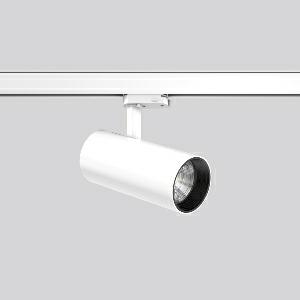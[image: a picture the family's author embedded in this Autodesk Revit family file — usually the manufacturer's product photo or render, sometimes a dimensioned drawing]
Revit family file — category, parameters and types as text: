
# Revit family: deecos_s_mini_742208_002_b176
name_source: partatom
category: Lighting Fixtures
units: mm (PartAtom-declared; Revit-internal decimal feet)

## family parameters
Cut with Voids When Loaded = No
Host = Face
Light Source = No
Part Type = Normal
Room Calculation Point = No
Round Connector Dimension = Use Diameter
Shared = No

## types (1)
- DEECOS S mini (1 x LED Modul 930, 2850 lm, 3000)
    Apparent Load = 29 VA
    Approval mark = CE
    CIE Flux Codes = 98 100 100 100 100
    Color Rendering = 90
    Color Temperature = 3000
    Default Elevation = 1800 mm
    Description = Series: DEECOS S mini
LED surface-mounted projector in modern design with no visible cooling ribs. Housing: die-cast aluminium, powder-coated. Rotation range: 356°. Swivel range: 90°. Black plastic ring and recessed LED to prevent glare from the side. Optical assembly with lens made of plastic (polycarbonate) for the best homogeneous light distribution - can be changed without tools. Best colour rendering index Ra>90. With multi adaptor for 3-circuit tracks 230 V. Suitable for Track on ceiling, Wall track. High quality converter without flickering and stroboscopic effect. The following accessories can be mounted without use of tools: interchangeable lenses, decorative glasses, honeycomb louvre, clear and frosted diffusers, white interchangeable plastic ring. 
Colour: traffic white, matt (RAL 9016)
Diameter: 87 mm
Height: 214 mm
Lamp: LED
Socket: without socket
Colour temperature: 3000K
Colour rendering index (CRI): 92
System power: 29 W
Rated luminous flux: 2850 lm
Luminous efficiency: 98 lm/W
Control gear: Regulated power supply
Protection class: I
Type of protection: IP 20
    Height = 214 mm
    Lamp = 1 x LED Modul 930
    Lamp Light Flux = 2850 lm
    Lamp count = 1
    Length = 87 mm
    Lifetime = 50000 h
    Luminous efficacy = 98 lm/W
    Manufacturer = RZB
    ModVariant = No
    Model = 742208.002
    Mounting Place = Ceiling
    Mounting Type = Rail mounted
    Number of Poles = 1
    OnlyDefault = Yes
    Power Factor = 1
    Product Name = DEECOS S mini
    Product group = Track mounted projectors
    ProductGroupID = 301
    Protection Class = Protection class I
    Protection Degree = IP 20
    RLX_Detail_Level = 1
    RLX_Emergency_Light_Flux = 0 lm
    RLX_Emergency_Type = 0
    RLX_Emergency_Type_DB = No
    RlxData = <blob elided: 35189 chars, md5=0dd4e1f8>
    Socket = socket
    Standby Power = 0 W
    System Light Flux = 2850 lm
    System Power = 29 W
    Type Comments = Product without accessories
    Type Image = 741930.002.jpg
    URL = http://relux.com
    VarID = ---
    Voltage = 230 V
    Voltage Range = 220-240 V
    Weight = 0.00 kg
    Width = 0 mm  [stored 0 ft]

note: [stored X ft] marks values corroborated as IEEE doubles in the binary element streams (Revit-internal decimal feet)

## geometry (parser evidence)
native form markers: Blend x4, Sweep x13
no freeform markers — native parametric forms only
